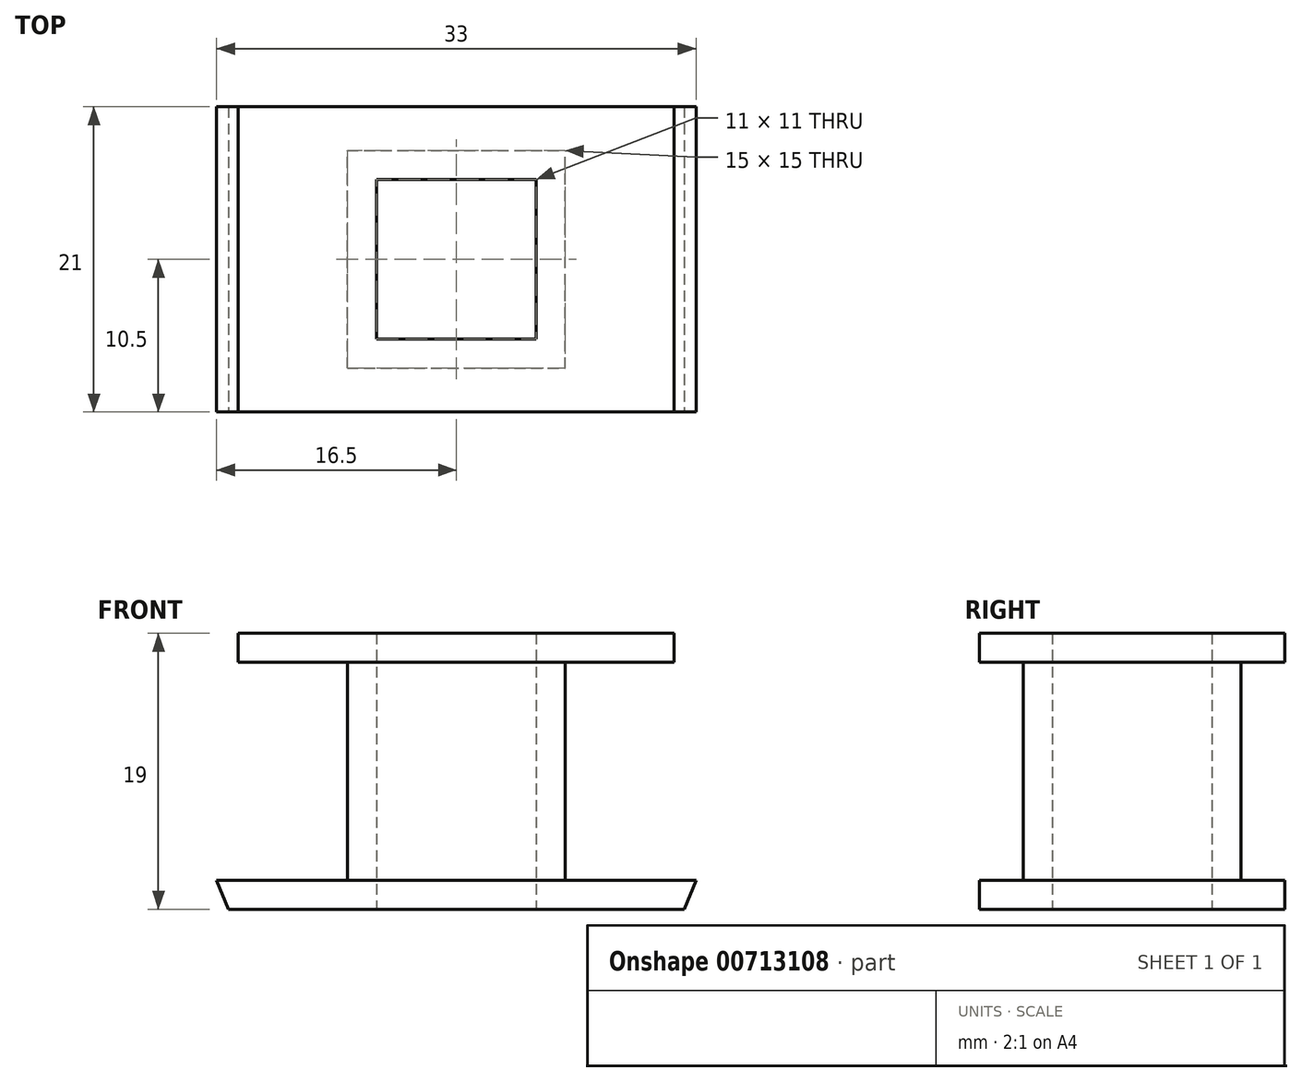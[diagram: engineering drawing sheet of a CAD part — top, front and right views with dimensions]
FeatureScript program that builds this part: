
annotation { "Feature Type Name" : "Feature", "Feature Type Description" : "" }
export const myFeature = defineFeature(function(context is Context, id is Id, definition is map)
    precondition{}
    {
        {
            var Q0;
            Q0=qCreatedBy(makeId("Top.planeOp"),FACE);
            var sketch = newSketch(context, id + "F0", { "sketchPlane" : qUnion([Q0])});
            skLineSegment(sketch, "E0.bottom", {"start": v(5.5, 5.5) * mm, "end": v(-5.5, 5.5) * mm});
            skLineSegment(sketch, "E0.top", {"start": v(5.5, -5.5) * mm, "end": v(-5.5, -5.5) * mm});
            skLineSegment(sketch, "E0.left", {"start": v(5.5, 5.5) * mm, "end": v(5.5, -5.5) * mm});
            skLineSegment(sketch, "E0.right", {"start": v(-5.5, 5.5) * mm, "end": v(-5.5, -5.5) * mm});
            skPoint(sketch, "E0.middle", {"position": v(0, 0) * mm});
            skLineSegment(sketch, "E1.bottom", {"start": v(7.5, 7.5) * mm, "end": v(-7.5, 7.5) * mm});
            skLineSegment(sketch, "E1.top", {"start": v(7.5, -7.5) * mm, "end": v(-7.5, -7.5) * mm});
            skLineSegment(sketch, "E1.left", {"start": v(7.5, 7.5) * mm, "end": v(7.5, -7.5) * mm});
            skLineSegment(sketch, "E1.right", {"start": v(-7.5, 7.5) * mm, "end": v(-7.5, -7.5) * mm});
            skLineSegment(sketch, "E2.bottom", {"start": v(16.5, 10.5) * mm, "end": v(-16.5, 10.5) * mm});
            skLineSegment(sketch, "E2.top", {"start": v(16.5, -10.5) * mm, "end": v(-16.5, -10.5) * mm});
            skLineSegment(sketch, "E2.left", {"start": v(16.5, 10.5) * mm, "end": v(16.5, -10.5) * mm});
            skLineSegment(sketch, "E2.right", {"start": v(-16.5, 10.5) * mm, "end": v(-16.5, -10.5) * mm});
            skSolve(sketch);
        }
        {
            var Q0;
            Q0=makeQuery(id+"F0.imprint","IMPRINT",FACE,{"disambiguationData":[TD([[makeQuery(id+"F0.imprint","IMPRINT",EDGE,{"derivedFrom":sQuery(id+"F0.wireOp",EDGE,"E1.bottom")}),-1.0]])]});
            var Q1;
            Q1=makeQuery(id+"F0.imprint","IMPRINT",FACE,{"disambiguationData":[TD([[makeQuery(id+"F0.imprint","IMPRINT",EDGE,{"derivedFrom":sQuery(id+"F0.wireOp",EDGE,"E0.bottom")}),-1.0]])]});
            extrude(context, id + "F1", {"entities" : qUnion([Q0, Q1]), "depth" : 2 * mm, "offsetDistance" : 25 * mm});
        }
        {
            var Q0;
            Q0=makeQuery(id+"F0.imprint","IMPRINT",FACE,{"disambiguationData":[TD([[makeQuery(id+"F0.imprint","IMPRINT",EDGE,{"derivedFrom":sQuery(id+"F0.wireOp",EDGE,"E0.bottom")}),-1.0]])]});
            extrude(context, id + "F2", {"entities" : qUnion([Q0]), "operationType" : NewBodyOperationType.ADD, "depth" : 17 * mm, "offsetDistance" : 25 * mm});
        }
        {
            var Q0;
            Q0=makeQuery(id+"F2.opExtrude","CAP_FACE",FACE,{"disambiguationData":[OSD([sQuery(id+"F0.wireOp",EDGE,"E0.bottom"),sQuery(id+"F0.wireOp",EDGE,"E0.top"),sQuery(id+"F0.wireOp",EDGE,"E0.left"),sQuery(id+"F0.wireOp",EDGE,"E0.right"),sQuery(id+"F0.wireOp",EDGE,"E1.bottom"),sQuery(id+"F0.wireOp",EDGE,"E1.top"),sQuery(id+"F0.wireOp",EDGE,"E1.left"),sQuery(id+"F0.wireOp",EDGE,"E1.right")])],"isStart":false});
            var sketch = newSketch(context, id + "F3", { "sketchPlane" : qUnion([Q0])});
            skLineSegment(sketch, "E3.bottom", {"start": v(5.5, 5.5) * mm, "end": v(-5.5, 5.5) * mm});
            skLineSegment(sketch, "E3.top", {"start": v(5.5, -5.5) * mm, "end": v(-5.5, -5.5) * mm});
            skLineSegment(sketch, "E3.left", {"start": v(5.5, 5.5) * mm, "end": v(5.5, -5.5) * mm});
            skLineSegment(sketch, "E3.right", {"start": v(-5.5, 5.5) * mm, "end": v(-5.5, -5.5) * mm});
            skPoint(sketch, "E3.middle", {"position": v(0, 0) * mm});
            skLineSegment(sketch, "E4.bottom", {"start": v(7.5, 7.5) * mm, "end": v(-7.5, 7.5) * mm});
            skLineSegment(sketch, "E4.top", {"start": v(7.5, -7.5) * mm, "end": v(-7.5, -7.5) * mm});
            skLineSegment(sketch, "E4.left", {"start": v(7.5, 7.5) * mm, "end": v(7.5, -7.5) * mm});
            skLineSegment(sketch, "E4.right", {"start": v(-7.5, 7.5) * mm, "end": v(-7.5, -7.5) * mm});
            skLineSegment(sketch, "E5.bottom", {"start": v(15, 10.5) * mm, "end": v(-15, 10.5) * mm});
            skLineSegment(sketch, "E5.top", {"start": v(15, -10.5) * mm, "end": v(-15, -10.5) * mm});
            skLineSegment(sketch, "E5.left", {"start": v(15, 10.5) * mm, "end": v(15, -10.5) * mm});
            skLineSegment(sketch, "E5.right", {"start": v(-15, 10.5) * mm, "end": v(-15, -10.5) * mm});
            skSolve(sketch);
        }
        {
            var Q0;
            Q0=makeQuery(id+"F3.imprint","IMPRINT",FACE,{"disambiguationData":[TD([[makeQuery(id+"F3.imprint","IMPRINT",EDGE,{"derivedFrom":sQuery(id+"F3.wireOp",EDGE,"E4.bottom")}),-1.0]])]});
            var Q1;
            Q1=makeQuery(id+"F3.imprint","IMPRINT",FACE,{"disambiguationData":[TD([[makeQuery(id+"F3.imprint","IMPRINT",EDGE,{"derivedFrom":sQuery(id+"F3.wireOp",EDGE,"E3.bottom")}),-1.0]])]});
            extrude(context, id + "F4", {"entities" : qUnion([Q0, Q1]), "operationType" : NewBodyOperationType.ADD, "depth" : 2 * mm, "offsetDistance" : 25 * mm});
        }
        {
            var Q0;
            Q0=makeQuery(id+"F1.opExtrude","SWEPT_FACE",FACE,{"disambiguationData":[OSD([sQuery(id+"F0.wireOp",EDGE,"E2.top")])]});
            var sketch = newSketch(context, id + "F5", { "sketchPlane" : qUnion([Q0])});
            skLineSegment(sketch, "E6", {"start": v(-16.5, 2) * mm, "end": v(-16.5, 0) * mm});
            skLineSegment(sketch, "E7", {"start": v(-16.5, 0) * mm, "end": v(-15.67, 0) * mm});
            skLineSegment(sketch, "E8", {"start": v(-15.67, 0) * mm, "end": v(-16.5, 2) * mm});
            skLineSegment(sketch, "E9", {"start": v(16.5, 2) * mm, "end": v(16.5, 0) * mm});
            skLineSegment(sketch, "E10", {"start": v(16.5, 0) * mm, "end": v(15.67, 0) * mm});
            skLineSegment(sketch, "E11", {"start": v(15.67, 0) * mm, "end": v(16.5, 2) * mm});
            skSolve(sketch);
        }
        {
            var Q0;
            Q0=makeQuery(id+"F5.imprint","IMPRINT",FACE,{"disambiguationData":[TD([[makeQuery(id+"F5.imprint","IMPRINT",EDGE,{"derivedFrom":sQuery(id+"F5.wireOp",EDGE,"E6")}),1.0]])]});
            var Q1;
            Q1=makeQuery(id+"F5.imprint","IMPRINT",FACE,{"disambiguationData":[TD([[makeQuery(id+"F5.imprint","IMPRINT",EDGE,{"derivedFrom":sQuery(id+"F5.wireOp",EDGE,"E9")}),-1.0]])]});
            extrude(context, id + "F6", {"entities" : qUnion([Q0, Q1]), "operationType" : NewBodyOperationType.REMOVE, "oppositeDirection" : true, "depth" : 25 * mm, "offsetDistance" : 25 * mm});
        }
    });
